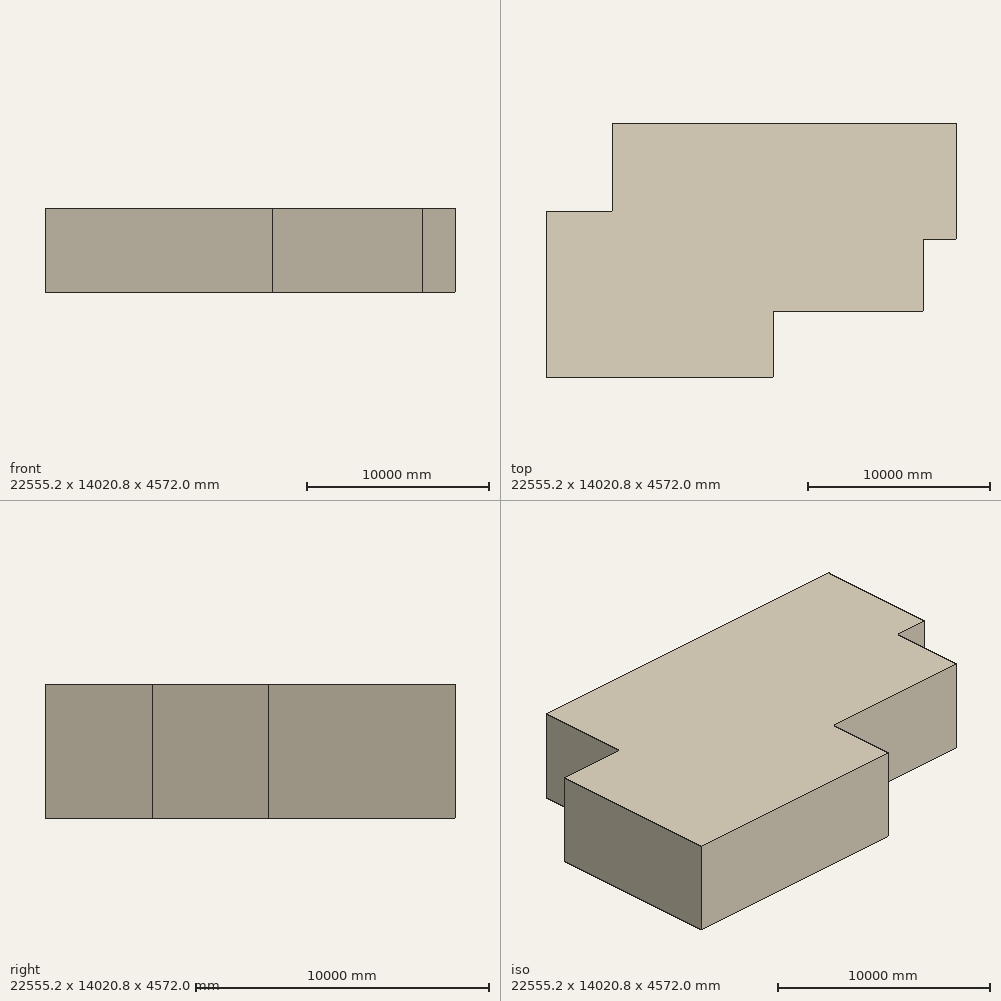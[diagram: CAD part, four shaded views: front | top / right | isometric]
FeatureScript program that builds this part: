
annotation { "Feature Type Name" : "Feature", "Feature Type Description" : "" }
export const myFeature = defineFeature(function(context is Context, id is Id, definition is map)
    precondition{}
    {
        {
            var Q0;
            Q0=qCreatedBy(makeId("Top.planeOp"),FACE);
            var sketch = newSketch(context, id + "F0", { "sketchPlane" : qUnion([Q0])});
            skLineSegment(sketch, "E0", {"start": v(0, 0) * mm, "end": v(-3657.6, 0) * mm});
            skLineSegment(sketch, "E1", {"start": v(-3657.6, 0) * mm, "end": v(-3657.6, -9144) * mm});
            skLineSegment(sketch, "E2", {"start": v(-3657.6, -9144) * mm, "end": v(8839.2, -9144) * mm});
            skLineSegment(sketch, "E3", {"start": v(0, 0) * mm, "end": v(0, 4876.8) * mm});
            skLineSegment(sketch, "E4", {"start": v(0, 4876.8) * mm, "end": v(18897.6, 4876.8) * mm});
            skLineSegment(sketch, "E5", {"start": v(18897.6, 4876.8) * mm, "end": v(18897.6, -1524) * mm});
            skLineSegment(sketch, "E6", {"start": v(18897.6, -1524) * mm, "end": v(17068.8, -1524) * mm});
            skLineSegment(sketch, "E7", {"start": v(17068.8, -1524) * mm, "end": v(17068.8, -5486.4) * mm});
            skLineSegment(sketch, "E8", {"start": v(17068.8, -5486.4) * mm, "end": v(8839.2, -5486.4) * mm});
            skLineSegment(sketch, "E9", {"start": v(8839.2, -9144) * mm, "end": v(8839.2, -5486.4) * mm});
            skSolve(sketch);
        }
        {
            var Q0;
            Q0 = qSketchRegion(id + "F0", true);
            extrude(context, id + "F1", {"entities" : qUnion([Q0]), "depth" : 4572 * mm, "offsetDistance" : 25.4 * mm});
        }
    });
